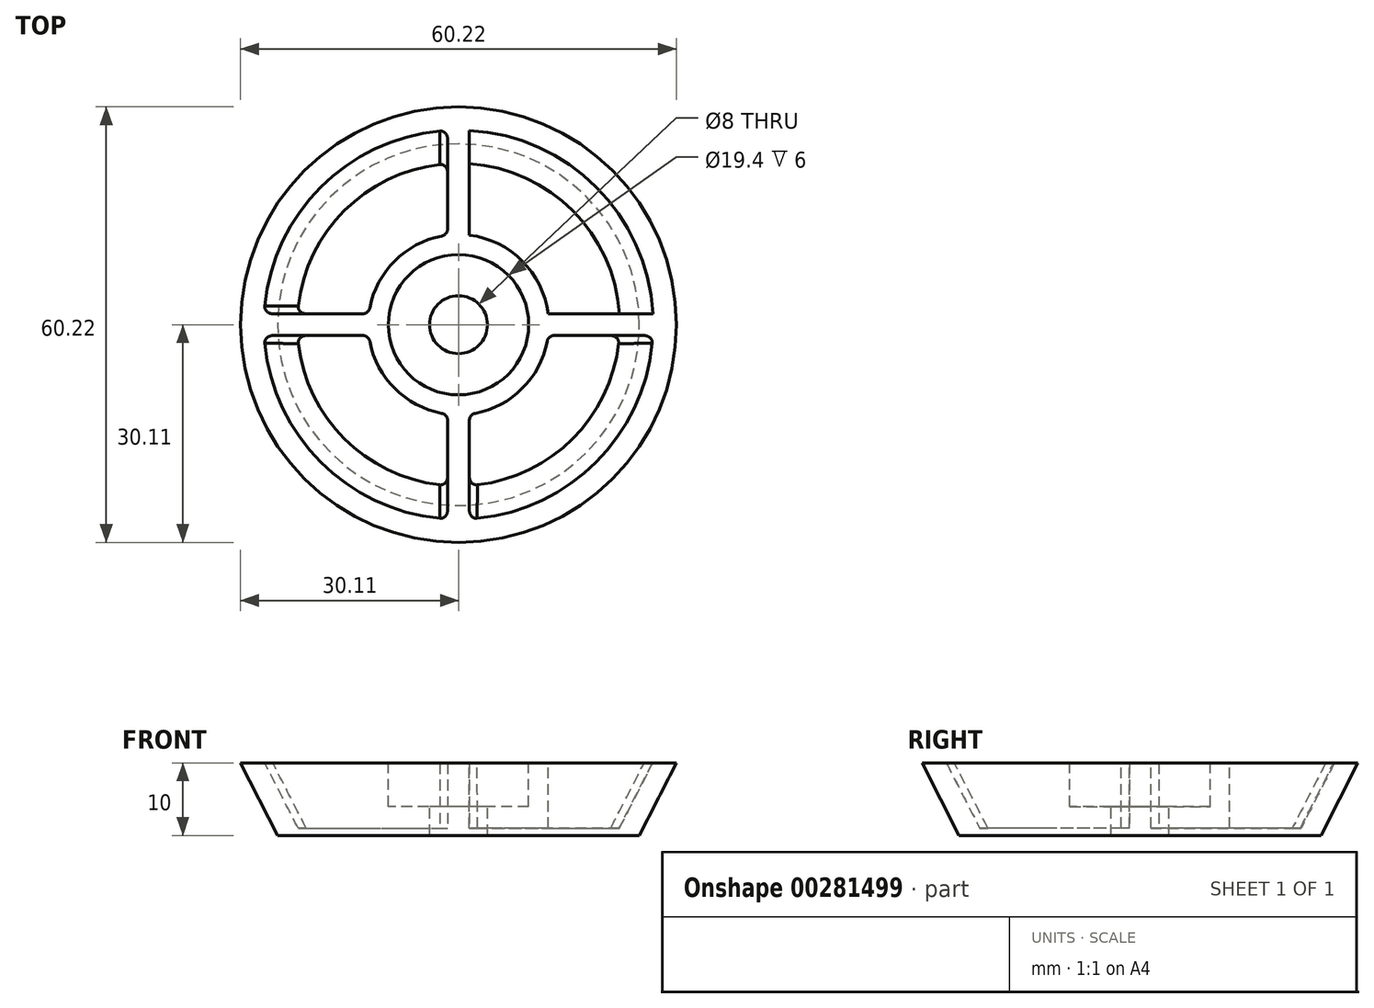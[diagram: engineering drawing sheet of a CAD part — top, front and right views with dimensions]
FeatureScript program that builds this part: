
annotation { "Feature Type Name" : "Feature", "Feature Type Description" : "" }
export const myFeature = defineFeature(function(context is Context, id is Id, definition is map)
    precondition{}
    {
        {
            var Q0;
            Q0=qCreatedBy(makeId("Front.planeOp"),FACE);
            var sketch = newSketch(context, id + "F0", { "sketchPlane" : qUnion([Q0])});
            skLineSegment(sketch, "E0", {"start": v(-25, 0) * mm, "end": v(-30.11, 10) * mm});
            skLineSegment(sketch, "E1", {"start": v(-30.11, 10) * mm, "end": v(-26.9, 10) * mm});
            skLineSegment(sketch, "E2", {"start": v(-26.9, 10) * mm, "end": v(-22.3, 1) * mm});
            skLineSegment(sketch, "E3", {"start": v(0, 24.99) * mm, "end": v(0, 0) * mm, "construction": true});
            skLineSegment(sketch, "E4", {"start": v(-9.7, 10) * mm, "end": v(-9.7, 4) * mm});
            skLineSegment(sketch, "E5", {"start": v(-9.7, 4) * mm, "end": v(-4, 4) * mm});
            skLineSegment(sketch, "E6", {"start": v(-4, 4) * mm, "end": v(-4, 0) * mm});
            skLineSegment(sketch, "E7", {"start": v(-9.7, 10) * mm, "end": v(-12.47, 10) * mm});
            skLineSegment(sketch, "E8", {"start": v(-12.47, 10) * mm, "end": v(-12.47, 1) * mm});
            skLineSegment(sketch, "E9", {"start": v(-22.3, 1) * mm, "end": v(-12.47, 1) * mm});
            skPoint(sketch, "E10.start.orphan", {"position": v(-21.8, 0) * mm});
            skPoint(sketch, "E11.start.orphan", {"position": v(-12.47, 0) * mm});
            skLineSegment(sketch, "E12", {"start": v(-25, 0) * mm, "end": v(-4, 0) * mm});
            skSolve(sketch);
        }
        {
            var Q0;
            Q0 = qSketchRegion(id + "F0", true);
            var Q1;
            Q1=sQuery(id+"F0.wireOp",EDGE,"E3");
            revolve(context, id + "F1", {"entities" : qUnion([Q0]), "axis" : qUnion([Q1]), "revolveType" : RevolveType.FULL});
        }
        {
            var Q0;
            Q0=makeQuery(id+"F1.opRevolve","SWEPT_FACE",FACE,{"disambiguationData":[OSD([sQuery(id+"F0.wireOp",EDGE,"E1")])]});
            var sketch = newSketch(context, id + "F2", { "sketchPlane" : qUnion([Q0])});
            skLineSegment(sketch, "E13.left", {"start": v(-1.5, 26.86) * mm, "end": v(-1.5, 12.38) * mm});
            skLineSegment(sketch, "E13.right", {"start": v(1.5, 26.86) * mm, "end": v(1.5, 12.38) * mm});
            skLineSegment(sketch, "E14.bottom", {"start": v(12.38, 1.5) * mm, "end": v(26.86, 1.5) * mm});
            skLineSegment(sketch, "E14.top", {"start": v(12.38, -1.5) * mm, "end": v(26.86, -1.5) * mm});
            skLineSegment(sketch, "E15.bottom", {"start": v(-26.86, 1.5) * mm, "end": v(-12.38, 1.5) * mm});
            skLineSegment(sketch, "E15.top", {"start": v(-26.86, -1.5) * mm, "end": v(-12.38, -1.5) * mm});
            skLineSegment(sketch, "E16.left", {"start": v(-1.5, -12.38) * mm, "end": v(-1.5, -26.86) * mm});
            skLineSegment(sketch, "E16.right", {"start": v(1.5, -12.38) * mm, "end": v(1.5, -26.86) * mm});
            skArc(sketch, "E17", {"start": v(-12.38, 1.5) * mm, "mid": v(-12.47, 0) * mm, "end": v(-12.38, -1.5) * mm});
            skArc(sketch, "E18", {"start": v(26.86, -1.5) * mm, "mid": v(26.9, 0) * mm, "end": v(26.86, 1.5) * mm});
            skArc(sketch, "E19.trimOffspring", {"start": v(1.5, 12.38) * mm, "mid": v(0, 12.47) * mm, "end": v(-1.5, 12.38) * mm});
            skArc(sketch, "E20.trimOffspring", {"start": v(12.38, -1.5) * mm, "mid": v(12.47, 0) * mm, "end": v(12.38, 1.5) * mm});
            skArc(sketch, "E21.trimOffspring", {"start": v(-1.5, -12.38) * mm, "mid": v(0, -12.47) * mm, "end": v(1.5, -12.38) * mm});
            skArc(sketch, "E22.trimOffspring", {"start": v(-1.5, -26.86) * mm, "mid": v(0, -26.9) * mm, "end": v(1.5, -26.86) * mm});
            skArc(sketch, "E23.trimOffspring", {"start": v(-26.86, 1.5) * mm, "mid": v(-26.9, 0) * mm, "end": v(-26.86, -1.5) * mm});
            skArc(sketch, "E24.trimOffspring", {"start": v(1.5, 26.86) * mm, "mid": v(0, 26.9) * mm, "end": v(-1.5, 26.86) * mm});
            skSolve(sketch);
        }
        {
            var Q0;
            Q0 = qSketchRegion(id + "F2", true);
            var Q1;
            Q1=makeQuery(id+"F1.opRevolve","SWEPT_FACE",FACE,{"disambiguationData":[OSD([sQuery(id+"F0.wireOp",EDGE,"E9")])]});
            extrude(context, id + "F3", {"entities" : qUnion([Q0]), "operationType" : NewBodyOperationType.ADD, "endBound" : BoundingType.UP_TO_NEXT, "oppositeDirection" : true, "endBoundEntityFace" : qUnion([Q1]), "depth" : 14.2 * mm});
        }
        {
            var Q0;
            Q0=makeQuery(id+"F3.opExtrude","TWEAK_EDGE",EDGE,{"derivedFrom":[makeQuery(id+"F1.opRevolve","SWEPT_FACE",FACE,{"disambiguationData":[OSD([sQuery(id+"F0.wireOp",EDGE,"E2")])]}),makeQuery(id+"F2.imprint","IMPRINT",EDGE,{"derivedFrom":sQuery(id+"F2.wireOp",EDGE,"E13.left")})]});
            var Q1;
            Q1=makeQuery(id+"F3.opExtrude","TWEAK_EDGE",EDGE,{"derivedFrom":[makeQuery(id+"F1.opRevolve","SWEPT_FACE",FACE,{"disambiguationData":[OSD([sQuery(id+"F0.wireOp",EDGE,"E2")])]}),makeQuery(id+"F2.imprint","IMPRINT",EDGE,{"derivedFrom":sQuery(id+"F2.wireOp",EDGE,"E13.right")})]});
            var Q2;
            Q2=makeQuery(id+"F3.opExtrude","TWEAK_EDGE",EDGE,{"derivedFrom":[makeQuery(id+"F1.opRevolve","SWEPT_FACE",FACE,{"disambiguationData":[OSD([sQuery(id+"F0.wireOp",EDGE,"E2")])]}),makeQuery(id+"F2.imprint","IMPRINT",EDGE,{"derivedFrom":sQuery(id+"F2.wireOp",EDGE,"E15.bottom")})]});
            var Q3;
            Q3=makeQuery(id+"F3.opExtrude","TWEAK_EDGE",EDGE,{"derivedFrom":[makeQuery(id+"F1.opRevolve","SWEPT_FACE",FACE,{"disambiguationData":[OSD([sQuery(id+"F0.wireOp",EDGE,"E2")])]}),makeQuery(id+"F2.imprint","IMPRINT",EDGE,{"derivedFrom":sQuery(id+"F2.wireOp",EDGE,"E15.top")})]});
            var Q4;
            Q4=makeQuery(id+"F3.opExtrude","TWEAK_EDGE",EDGE,{"derivedFrom":[makeQuery(id+"F1.opRevolve","SWEPT_FACE",FACE,{"disambiguationData":[OSD([sQuery(id+"F0.wireOp",EDGE,"E2")])]}),makeQuery(id+"F2.imprint","IMPRINT",EDGE,{"derivedFrom":sQuery(id+"F2.wireOp",EDGE,"E16.left")})]});
            var Q5;
            Q5=makeQuery(id+"F3.opExtrude","TWEAK_EDGE",EDGE,{"derivedFrom":[makeQuery(id+"F1.opRevolve","SWEPT_FACE",FACE,{"disambiguationData":[OSD([sQuery(id+"F0.wireOp",EDGE,"E2")])]}),makeQuery(id+"F2.imprint","IMPRINT",EDGE,{"derivedFrom":sQuery(id+"F2.wireOp",EDGE,"E14.bottom")})]});
            var Q6;
            Q6=makeQuery(id+"F3.opExtrude","TWEAK_EDGE",EDGE,{"derivedFrom":[makeQuery(id+"F1.opRevolve","SWEPT_FACE",FACE,{"disambiguationData":[OSD([sQuery(id+"F0.wireOp",EDGE,"E2")])]}),makeQuery(id+"F2.imprint","IMPRINT",EDGE,{"derivedFrom":sQuery(id+"F2.wireOp",EDGE,"E14.top")})]});
            var Q7;
            Q7=makeQuery(id+"F3.opExtrude","TWEAK_EDGE",EDGE,{"derivedFrom":[makeQuery(id+"F1.opRevolve","SWEPT_FACE",FACE,{"disambiguationData":[OSD([sQuery(id+"F0.wireOp",EDGE,"E2")])]}),makeQuery(id+"F2.imprint","IMPRINT",EDGE,{"derivedFrom":sQuery(id+"F2.wireOp",EDGE,"E16.right")})]});
            var Q8;
            Q8=makeQuery(id+"F3.opExtrude","SWEPT_EDGE",EDGE,{"disambiguationData":[OSD([sQuery(id+"F2.wireOp",EDGE,"E13.right"),sQuery(id+"F2.wireOp",EDGE,"E19.trimOffspring")])]});
            var Q9;
            Q9=makeQuery(id+"F3.opExtrude","SWEPT_EDGE",EDGE,{"disambiguationData":[OSD([sQuery(id+"F2.wireOp",EDGE,"E14.bottom"),sQuery(id+"F2.wireOp",EDGE,"E20.trimOffspring")])]});
            var Q10;
            Q10=makeQuery(id+"F3.opExtrude","SWEPT_EDGE",EDGE,{"disambiguationData":[OSD([sQuery(id+"F2.wireOp",EDGE,"E14.top"),sQuery(id+"F2.wireOp",EDGE,"E20.trimOffspring")])]});
            var Q11;
            Q11=makeQuery(id+"F3.opExtrude","SWEPT_EDGE",EDGE,{"disambiguationData":[OSD([sQuery(id+"F2.wireOp",EDGE,"E16.right"),sQuery(id+"F2.wireOp",EDGE,"E21.trimOffspring")])]});
            var Q12;
            Q12=makeQuery(id+"F3.opExtrude","SWEPT_EDGE",EDGE,{"disambiguationData":[OSD([sQuery(id+"F2.wireOp",EDGE,"E16.left"),sQuery(id+"F2.wireOp",EDGE,"E21.trimOffspring")])]});
            var Q13;
            Q13=makeQuery(id+"F3.opExtrude","SWEPT_EDGE",EDGE,{"disambiguationData":[OSD([sQuery(id+"F2.wireOp",EDGE,"E15.top"),sQuery(id+"F2.wireOp",EDGE,"E17")])]});
            var Q14;
            Q14=makeQuery(id+"F3.opExtrude","SWEPT_EDGE",EDGE,{"disambiguationData":[OSD([sQuery(id+"F2.wireOp",EDGE,"E15.bottom"),sQuery(id+"F2.wireOp",EDGE,"E17")])]});
            var Q15;
            Q15=makeQuery(id+"F3.opExtrude","SWEPT_EDGE",EDGE,{"disambiguationData":[OSD([sQuery(id+"F2.wireOp",EDGE,"E13.left"),sQuery(id+"F2.wireOp",EDGE,"E19.trimOffspring")])]});
            fillet(context, id + "F4", {"entities" : qUnion([Q0, Q1, Q2, Q3, Q4, Q5, Q6, Q7, Q8, Q9, Q10, Q11, Q12, Q13, Q14, Q15]), "radius" : 1 * mm, "tangentPropagation" : true, "allowEdgeOverflow" : false});
        }
    });
